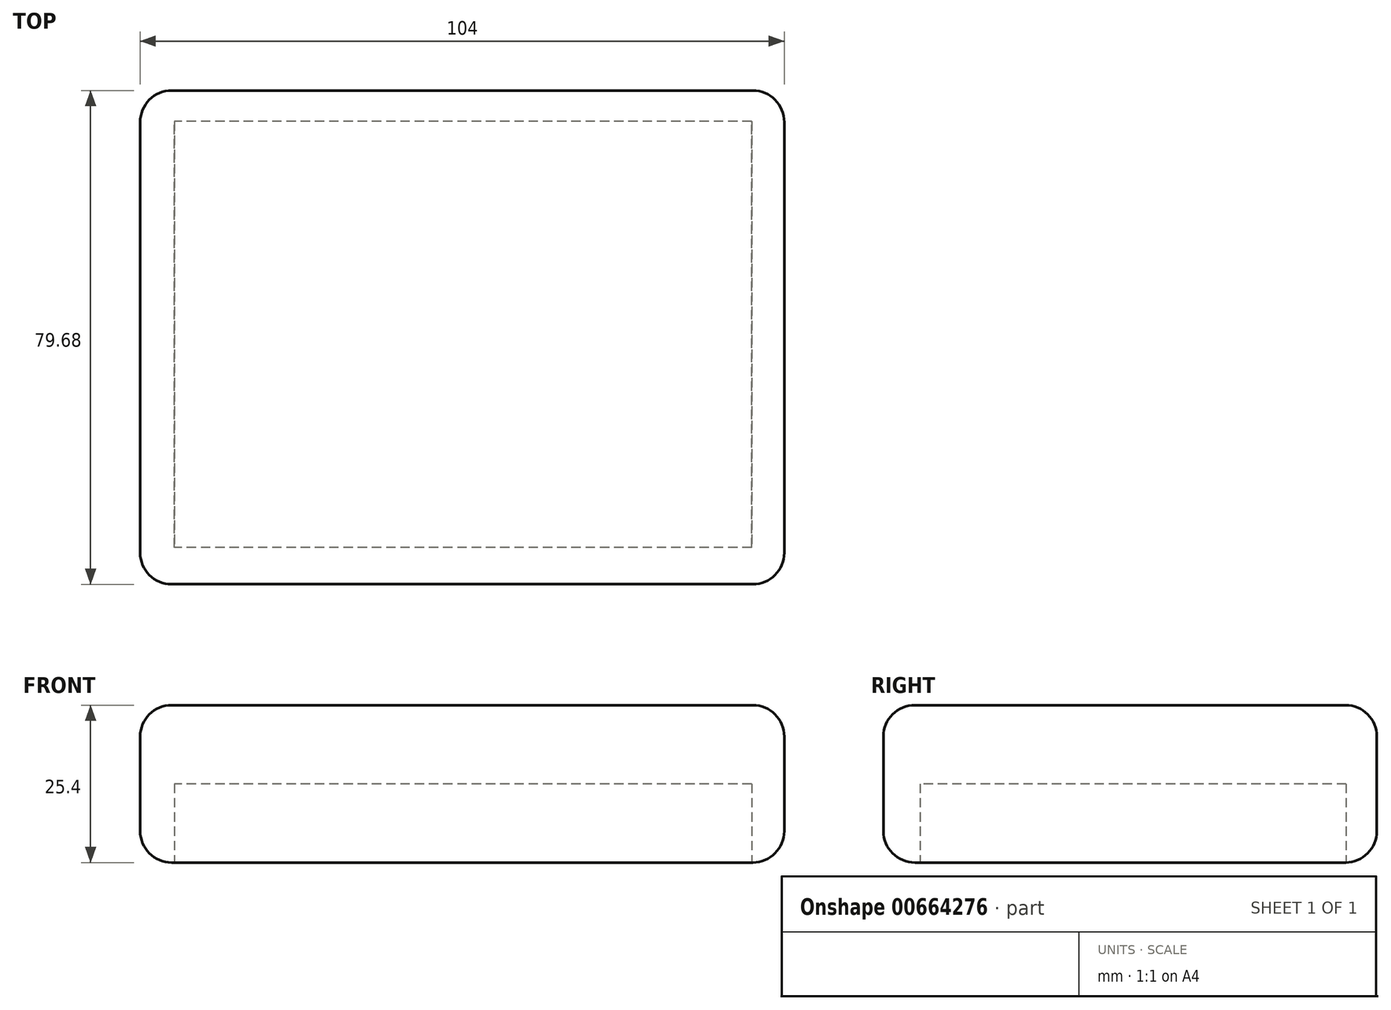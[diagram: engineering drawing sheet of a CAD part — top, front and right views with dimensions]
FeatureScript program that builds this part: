
annotation { "Feature Type Name" : "Feature", "Feature Type Description" : "" }
export const myFeature = defineFeature(function(context is Context, id is Id, definition is map)
    precondition{}
    {
        {
            var Q0;
            Q0=qCreatedBy(makeId("Top.planeOp"),FACE);
            var sketch = newSketch(context, id + "F0", { "sketchPlane" : qUnion([Q0])});
            skLineSegment(sketch, "E0.bottom", {"start": v(52, 39.84) * mm, "end": v(-52, 39.84) * mm});
            skLineSegment(sketch, "E0.top", {"start": v(52, -39.84) * mm, "end": v(-52, -39.84) * mm});
            skLineSegment(sketch, "E0.left", {"start": v(52, 39.84) * mm, "end": v(52, -39.84) * mm});
            skLineSegment(sketch, "E0.right", {"start": v(-52, 39.84) * mm, "end": v(-52, -39.84) * mm});
            skPoint(sketch, "E0.middle", {"position": v(0, 0) * mm});
            skSolve(sketch);
        }
        {
            var Q0;
            Q0 = qSketchRegion(id + "F0", true);
            extrude(context, id + "F1", {"entities" : qUnion([Q0]), "depth" : 25.4 * mm, "offsetDistance" : 25.4 * mm});
        }
        {
            var Q0;
            Q0=makeQuery(id+"F1.opExtrude","SWEPT_EDGE",EDGE,{"disambiguationData":[OSD([sQuery(id+"F0.wireOp",EDGE,"E0.bottom"),sQuery(id+"F0.wireOp",EDGE,"E0.left")])]});
            var Q1;
            Q1=makeQuery(id+"F1.opExtrude","CAP_EDGE",EDGE,{"disambiguationData":[OSD([sQuery(id+"F0.wireOp",EDGE,"E0.bottom")])],"isStart":false});
            var Q2;
            Q2=makeQuery(id+"F1.opExtrude","CAP_EDGE",EDGE,{"disambiguationData":[OSD([sQuery(id+"F0.wireOp",EDGE,"E0.left")])],"isStart":false});
            var Q3;
            Q3=makeQuery(id+"F1.opExtrude","CAP_EDGE",EDGE,{"disambiguationData":[OSD([sQuery(id+"F0.wireOp",EDGE,"E0.right")])],"isStart":false});
            var Q4;
            Q4=makeQuery(id+"F1.opExtrude","CAP_EDGE",EDGE,{"disambiguationData":[OSD([sQuery(id+"F0.wireOp",EDGE,"E0.top")])],"isStart":false});
            var Q5;
            Q5=makeQuery(id+"F1.opExtrude","CAP_EDGE",EDGE,{"disambiguationData":[OSD([sQuery(id+"F0.wireOp",EDGE,"E0.top")])],"isStart":true});
            var Q6;
            Q6=makeQuery(id+"F1.opExtrude","SWEPT_EDGE",EDGE,{"disambiguationData":[OSD([sQuery(id+"F0.wireOp",EDGE,"E0.top"),sQuery(id+"F0.wireOp",EDGE,"E0.left")])]});
            var Q7;
            Q7=makeQuery(id+"F1.opExtrude","SWEPT_EDGE",EDGE,{"disambiguationData":[OSD([sQuery(id+"F0.wireOp",EDGE,"E0.top"),sQuery(id+"F0.wireOp",EDGE,"E0.right")])]});
            var Q8;
            Q8=makeQuery(id+"F1.opExtrude","CAP_EDGE",EDGE,{"disambiguationData":[OSD([sQuery(id+"F0.wireOp",EDGE,"E0.right")])],"isStart":true});
            var Q9;
            Q9=makeQuery(id+"F1.opExtrude","CAP_EDGE",EDGE,{"disambiguationData":[OSD([sQuery(id+"F0.wireOp",EDGE,"E0.bottom")])],"isStart":true});
            var Q10;
            Q10=makeQuery(id+"F1.opExtrude","CAP_EDGE",EDGE,{"disambiguationData":[OSD([sQuery(id+"F0.wireOp",EDGE,"E0.left")])],"isStart":true});
            fillet(context, id + "F2", {"entities" : qUnion([Q0, Q1, Q2, Q3, Q4, Q5, Q6, Q7, Q8, Q9, Q10]), "radius" : 5.08 * mm, "tangentPropagation" : true, "allowEdgeOverflow" : false});
        }
        {
            var Q0;
            Q0=makeQuery(id+"F1.opExtrude","CAP_FACE",FACE,{"disambiguationData":[OSD([sQuery(id+"F0.wireOp",EDGE,"E0.bottom"),sQuery(id+"F0.wireOp",EDGE,"E0.top"),sQuery(id+"F0.wireOp",EDGE,"E0.left"),sQuery(id+"F0.wireOp",EDGE,"E0.right")])],"isStart":true});
            var sketch = newSketch(context, id + "F3", { "sketchPlane" : qUnion([Q0])});
            skLineSegment(sketch, "E1.bottom", {"start": v(46.92, -34.76) * mm, "end": v(-46.92, -34.76) * mm});
            skLineSegment(sketch, "E1.top", {"start": v(46.92, 34.76) * mm, "end": v(-46.92, 34.76) * mm});
            skLineSegment(sketch, "E1.left", {"start": v(46.92, -34.76) * mm, "end": v(46.92, 34.76) * mm});
            skLineSegment(sketch, "E1.right", {"start": v(-46.92, -34.76) * mm, "end": v(-46.92, 34.76) * mm});
            skSolve(sketch);
        }
        {
            var Q0;
            Q0=makeQuery(id+"F3.imprint","IMPRINT",FACE,{"disambiguationData":[TD([[makeQuery(id+"F3.imprint","IMPRINT",EDGE,{"derivedFrom":sQuery(id+"F3.wireOp",EDGE,"E1.bottom")}),1.0]])]});
            var sketch = newSketch(context, id + "F4", { "sketchPlane" : qUnion([Q0])});
            skLineSegment(sketch, "E2.bottom", {"start": v(46.73, -34.87) * mm, "end": v(-46.48, -34.87) * mm});
            skLineSegment(sketch, "E2.top", {"start": v(46.73, 33.9) * mm, "end": v(-46.48, 33.9) * mm});
            skLineSegment(sketch, "E2.left", {"start": v(46.73, -34.87) * mm, "end": v(46.73, 33.9) * mm});
            skLineSegment(sketch, "E2.right", {"start": v(-46.48, -34.87) * mm, "end": v(-46.48, 33.9) * mm});
            skSolve(sketch);
        }
        {
            var Q0;
            Q0 = qSketchRegion(id + "F4", true);
            extrude(context, id + "F5", {"entities" : qUnion([Q0]), "operationType" : NewBodyOperationType.REMOVE, "oppositeDirection" : true, "depth" : 12.7 * mm, "offsetDistance" : 25.4 * mm});
        }
        {
            var Q0;
            Q0=makeQuery(id+"F1.opExtrude","SWEPT_EDGE",EDGE,{"disambiguationData":[OSD([sQuery(id+"F0.wireOp",EDGE,"E0.bottom"),sQuery(id+"F0.wireOp",EDGE,"E0.right")])]});
            fillet(context, id + "F6", {"entities" : qUnion([Q0]), "radius" : 5.08 * mm, "tangentPropagation" : true, "allowEdgeOverflow" : false});
        }
    });
